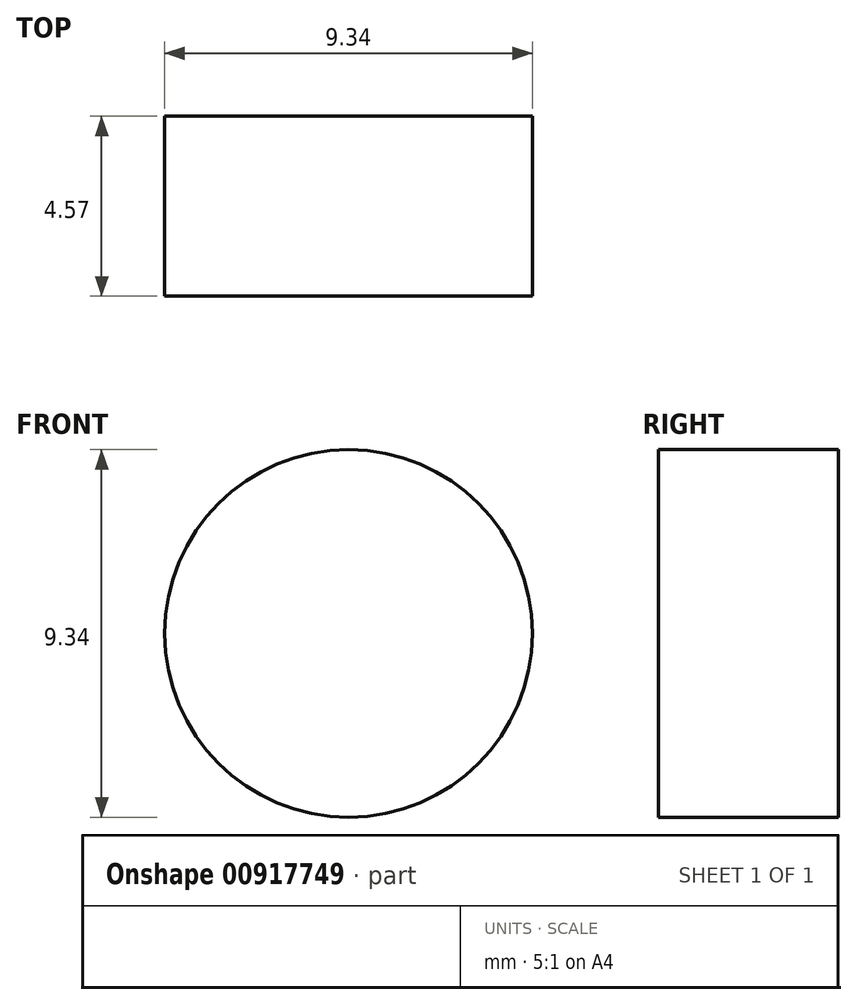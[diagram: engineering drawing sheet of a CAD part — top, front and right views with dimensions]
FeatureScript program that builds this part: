
annotation { "Feature Type Name" : "Feature", "Feature Type Description" : "" }
export const myFeature = defineFeature(function(context is Context, id is Id, definition is map)
    precondition{}
    {
        {
            var Q0;
            Q0=qCreatedBy(makeId("Front.planeOp"),FACE);
            var sketch = newSketch(context, id + "F0", { "sketchPlane" : qUnion([Q0])});
            skArc(sketch, "E0", {"start": v(0, -47.61) * mm, "mid": v(47.61, 0) * mm, "end": v(0, 47.61) * mm});
            skLineSegment(sketch, "E1", {"start": v(0, 47.61) * mm, "end": v(0, -47.61) * mm});
            skSolve(sketch);
        }
        {
            var Q0;
            Q0 = qSketchRegion(id + "F0", true);
            var Q1;
            Q1=sQuery(id+"F0.wireOp",EDGE,"E1");
            revolve(context, id + "F1", {"surfaceOperationType" : NewSurfaceOperationType.NEW, "entities" : qUnion([Q0]), "axis" : qUnion([Q1]), "revolveType" : RevolveType.ONE_DIRECTION, "angle" : 180 * degree});
        }
        {
            var Q0;
            Q0=makeQuery(id+"F1.opRevolve","CAP_FACE",FACE,{"disambiguationData":[OSD([sQuery(id+"F0.wireOp",EDGE,"E0"),sQuery(id+"F0.wireOp",EDGE,"E1")])],"isStart":true});
            shell(context, id + "F2", {"entities" : qUnion([Q0]), "thickness" : 4.57 * mm});
        }
        {
            var Q0;
            Q0=makeQuery(id+"F1.opRevolve","CAP_FACE",FACE,{"disambiguationData":[OSD([sQuery(id+"F0.wireOp",EDGE,"E0"),sQuery(id+"F0.wireOp",EDGE,"E1")])],"isStart":true});
            var sketch = newSketch(context, id + "F3", { "sketchPlane" : qUnion([Q0])});
            skCircle(sketch, "E2", {"center": v(0, 0) * mm, "radius": 46.34 * mm});
            skCircle(sketch, "E3", {"center": v(0, 0) * mm, "radius": 44.31 * mm});
            skLineSegment(sketch, "E4", {"start": v(0, 43.04) * mm, "end": v(0, 44.31) * mm, "construction": true});
            skLineSegment(sketch, "E5", {"start": v(0, 46.34) * mm, "end": v(0, 47.61) * mm, "construction": true});
            skSolve(sketch);
        }
        {
            var Q0;
            Q0=makeQuery(id+"F3.imprint","IMPRINT",FACE,{"disambiguationData":[TD([[makeQuery(id+"F3.imprint","IMPRINT",EDGE,{"derivedFrom":sQuery(id+"F3.wireOp",EDGE,"E2")}),1.0]])]});
            extrude(context, id + "F4", {"entities" : qUnion([Q0]), "operationType" : NewBodyOperationType.REMOVE, "oppositeDirection" : true, "depth" : 6.63 * mm, "offsetDistance" : 25.4 * mm});
        }
        {
            var Q0;
            Q0=makeQuery(id+"F1.opRevolve","CAP_FACE",FACE,{"disambiguationData":[OSD([sQuery(id+"F0.wireOp",EDGE,"E0"),sQuery(id+"F0.wireOp",EDGE,"E1")])],"isStart":true});
            var sketch = newSketch(context, id + "F5", { "sketchPlane" : qUnion([Q0])});
            skLineSegment(sketch, "E6.bottom", {"start": v(0.44, 47.23) * mm, "end": v(-0.44, 47.23) * mm});
            skLineSegment(sketch, "E6.top", {"start": v(0.44, 43.42) * mm, "end": v(-0.44, 43.42) * mm});
            skLineSegment(sketch, "E6.left", {"start": v(0.44, 47.23) * mm, "end": v(0.44, 43.42) * mm});
            skLineSegment(sketch, "E6.right", {"start": v(-0.44, 47.23) * mm, "end": v(-0.44, 43.42) * mm});
            skPoint(sketch, "E6.middle", {"position": v(0, 45.33) * mm});
            skLineSegment(sketch, "E7", {"start": v(0, 47.61) * mm, "end": v(0, 47.23) * mm, "construction": true});
            skLineSegment(sketch, "E8", {"start": v(0, 43.42) * mm, "end": v(0, 43.04) * mm, "construction": true});
            skSolve(sketch);
        }
        {
            var Q0;
            Q0 = qSketchRegion(id + "F5", true);
            extrude(context, id + "F6", {"entities" : qUnion([Q0]), "operationType" : NewBodyOperationType.REMOVE, "oppositeDirection" : true, "depth" : 6.63 * mm, "offsetDistance" : 25.4 * mm});
        }
        {
            var Q0;
            Q0=qCreatedBy(makeId("Front.planeOp"),FACE);
            cPlane(context, id + "F7", {"entities" : qUnion([Q0]), "cplaneType" : CPlaneType.OFFSET, "offset" : 47.6 * mm, "width" : 152.4 * mm, "height" : 152.4 * mm});
        }
        {
            var Q0;
            Q0=qCreatedBy(id+"F7.planeOp",FACE);
            var sketch = newSketch(context, id + "F8", { "sketchPlane" : qUnion([Q0])});
            skLineSegment(sketch, "E9.bottom", {"start": v(127, -127) * mm, "end": v(-127, -127) * mm});
            skLineSegment(sketch, "E9.top", {"start": v(127, 127) * mm, "end": v(-127, 127) * mm});
            skLineSegment(sketch, "E9.left", {"start": v(127, -127) * mm, "end": v(127, 127) * mm});
            skLineSegment(sketch, "E9.right", {"start": v(-127, -127) * mm, "end": v(-127, 127) * mm});
            skPoint(sketch, "E9.middle", {"position": v(0, 0) * mm});
            skSolve(sketch);
        }
        {
            var Q0;
            Q0 = qSketchRegion(id + "F8", true);
            extrude(context, id + "F9", {"entities" : qUnion([Q0]), "operationType" : NewBodyOperationType.REMOVE, "oppositeDirection" : true, "depth" : 4.83 * mm, "offsetDistance" : 25.4 * mm});
        }
        {
            var Q0;
            Q0 = qSketchRegion(id + "F8", true);
            extrude(context, id + "F10", {"entities" : qUnion([Q0]), "operationType" : NewBodyOperationType.REMOVE, "oppositeDirection" : true, "depth" : 3.3 * mm, "offsetDistance" : 25.4 * mm});
        }
        {
            var Q0;
            Q0=makeQuery(id+"F9.boolean.opBoolean","COPY",FACE,{"derivedFrom":makeQuery(id+"F9.opExtrude","CAP_FACE",FACE,{"disambiguationData":[OSD([sQuery(id+"F8.wireOp",EDGE,"E9.bottom"),sQuery(id+"F8.wireOp",EDGE,"E9.top"),sQuery(id+"F8.wireOp",EDGE,"E9.left"),sQuery(id+"F8.wireOp",EDGE,"E9.right")])],"isStart":false})});
            var sketch = newSketch(context, id + "F11", { "sketchPlane" : qUnion([Q0])});
            skCircle(sketch, "E10", {"center": v(0, 0) * mm, "radius": 4.67 * mm});
            skSolve(sketch);
        }
        {
            var Q0;
            Q0 = qSketchRegion(id + "F11", true);
            var Q1;
            {var subQ0=makeQuery(id+"F9.opExtrude","CAP_FACE",FACE,{"disambiguationData":[OSD([sQuery(id+"F8.wireOp",EDGE,"E9.bottom"),sQuery(id+"F8.wireOp",EDGE,"E9.top"),sQuery(id+"F8.wireOp",EDGE,"E9.left"),sQuery(id+"F8.wireOp",EDGE,"E9.right")])],"isStart":false});var subQ1=sQuery(id+"F0.wireOp",EDGE,"E0");Q1=makeQuery(id+"F11.imprint","IMPRINT",FACE,{"disambiguationData":[TD([[makeQuery(id+"F11.imprint","IMPRINT",EDGE,{"derivedFrom":makeQuery(id+"F9.boolean.opBoolean","INTERSECT",EDGE,{"derivedFrom":[makeQuery(id+"F2.opShell","OFFSET_FACE",FACE,{"disambiguationData":[OSD([subQ1])]}),subQ0]})}),-1.0]])]});}
            var Q2;
            Q2=makeQuery(id+"F9.boolean.opBoolean","COPY",FACE,{"derivedFrom":makeQuery(id+"F9.opExtrude","CAP_FACE",FACE,{"disambiguationData":[OSD([sQuery(id+"F8.wireOp",EDGE,"E9.bottom"),sQuery(id+"F8.wireOp",EDGE,"E9.top"),sQuery(id+"F8.wireOp",EDGE,"E9.left"),sQuery(id+"F8.wireOp",EDGE,"E9.right")])],"isStart":false})});
            extrude(context, id + "F12", {"entities" : qUnion([Q0, Q1]), "operationType" : NewBodyOperationType.ADD, "oppositeDirection" : true, "depth" : 4.57 * mm, "endBoundEntityFace" : qUnion([Q2]), "offsetDistance" : 25.4 * mm});
        }
        {
            var Q0;
            Q0=makeQuery(id+"F9.boolean.opBoolean","SPLIT",BODY,{"disambiguationData":[OD(1.0)],"derivedFrom":makeQuery(id+"F1.opRevolve","SWEPT_BODY",BODY,{"disambiguationData":[OSD([sQuery(id+"F0.wireOp",EDGE,"E0"),sQuery(id+"F0.wireOp",EDGE,"E1")])]})});
            deleteBodies(context, id + "F13", {"entities" : qUnion([Q0])});
        }
    });
